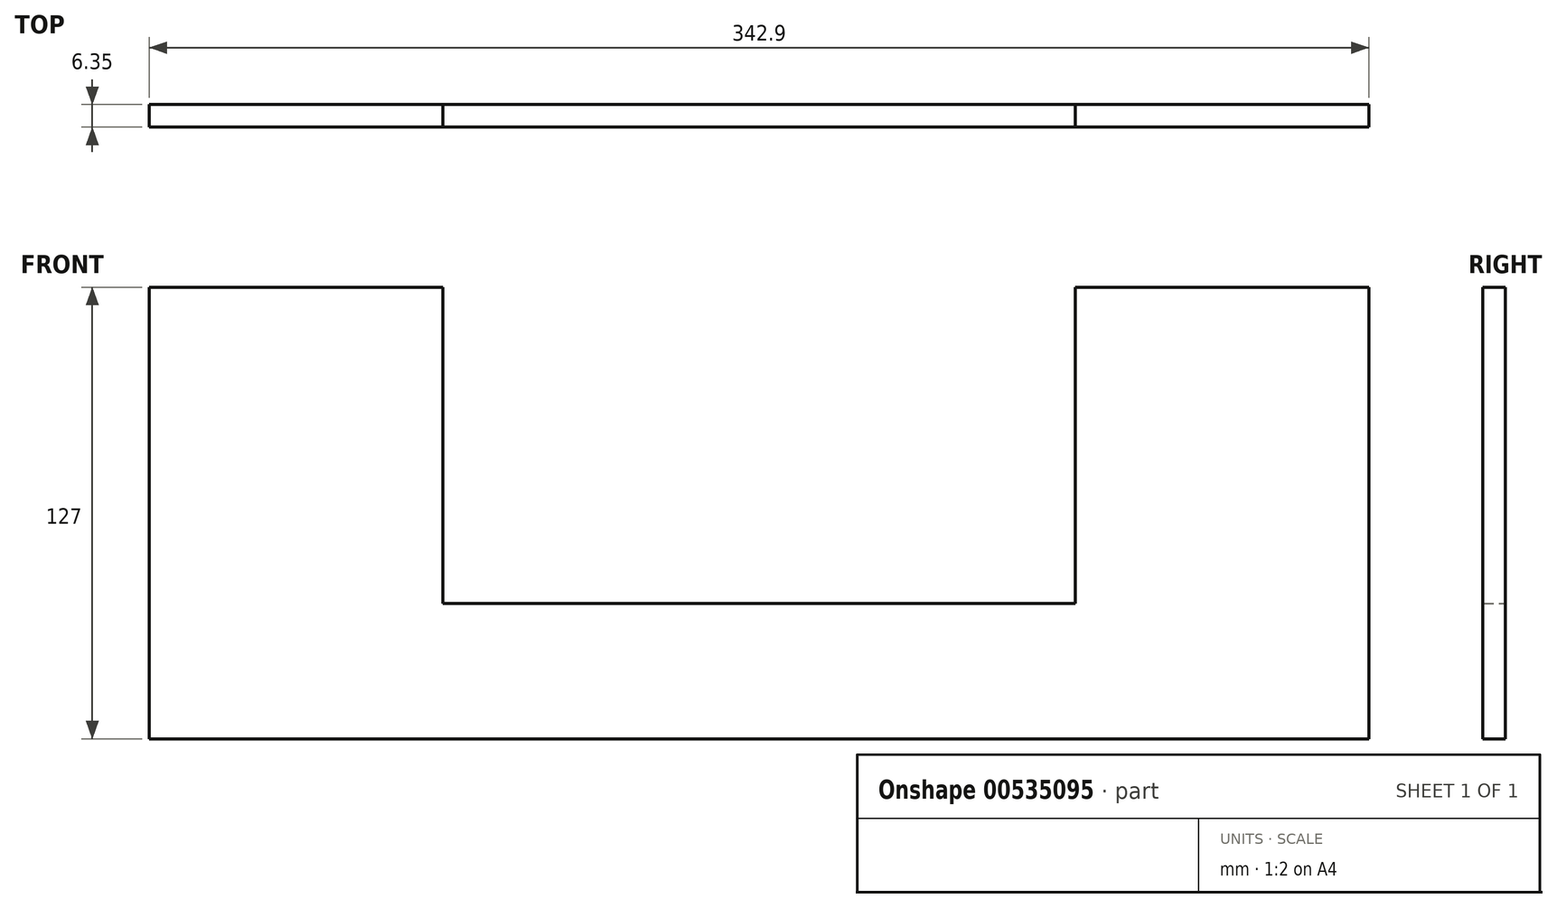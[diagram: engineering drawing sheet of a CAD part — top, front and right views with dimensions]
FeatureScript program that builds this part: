
annotation { "Feature Type Name" : "Feature", "Feature Type Description" : "" }
export const myFeature = defineFeature(function(context is Context, id is Id, definition is map)
    precondition{}
    {
        {
            var Q0;
            Q0=qCreatedBy(makeId("Front.planeOp"),FACE);
            var sketch = newSketch(context, id + "F0", { "sketchPlane" : qUnion([Q0])});
            skLineSegment(sketch, "E0.bottom", {"start": v(0, 0) * mm, "end": v(-171.45, 0) * mm});
            skLineSegment(sketch, "E0.top", {"start": v(-88.9, 127) * mm, "end": v(-171.45, 127) * mm});
            skLineSegment(sketch, "E0.right", {"start": v(-171.45, 0) * mm, "end": v(-171.45, 127) * mm});
            skLineSegment(sketch, "E1.top", {"start": v(-88.9, 38.1) * mm, "end": v(0, 38.1) * mm});
            skLineSegment(sketch, "E1.left", {"start": v(-88.9, 127) * mm, "end": v(-88.9, 38.1) * mm});
            skLineSegment(sketch, "E2.MirrorCS", {"start": v(88.9, 38.1) * mm, "end": v(0, 38.1) * mm});
            skLineSegment(sketch, "E3.MirrorCS", {"start": v(88.9, 127) * mm, "end": v(88.9, 38.1) * mm});
            skLineSegment(sketch, "E4.MirrorCS", {"start": v(88.9, 127) * mm, "end": v(171.45, 127) * mm});
            skLineSegment(sketch, "E5.MirrorCS", {"start": v(171.45, 0) * mm, "end": v(171.45, 127) * mm});
            skLineSegment(sketch, "E6.MirrorCS", {"start": v(0, 0) * mm, "end": v(171.45, 0) * mm});
            skSolve(sketch);
        }
        {
            var Q0;
            Q0=makeQuery(id+"F0.imprint","IMPRINT",FACE,{"disambiguationData":[TD([[makeQuery(id+"F0.imprint","IMPRINT",EDGE,{"derivedFrom":sQuery(id+"F0.wireOp",EDGE,"E0.bottom")}),-1.0]])]});
            extrude(context, id + "F1", {"entities" : qUnion([Q0]), "depth" : 6.35 * mm, "offsetDistance" : 25.4 * mm});
        }
    });
